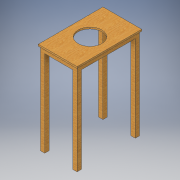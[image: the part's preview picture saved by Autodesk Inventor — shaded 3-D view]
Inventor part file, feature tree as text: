
AUTODESK INVENTOR PART (.ipt)
format: ipt  version: 2018 (Build 220112000, 112)  size: 184,320 bytes
history: native  units: in
note: dims shown in document units (in); Inventor stores cm internally (conversion verified against a paired STEP export)
features: extrude x4, sketch x4
ambient origin geometry x8: Origin, YZ Plane, XZ Plane, XY Plane, X Axis, Y Axis, Z Axis, Center Point
bodies: Solid1 (feature_tree)
feature tree (8):
  extrude  "Extrusion1"  Depth=60.0in
  extrude  "Extrusion2"  Depth=30.0in
  extrude  "Extrusion3"  Depth=4.0in
  extrude  "Extrusion4"  Depth=4.0in
  sketch  "Sketch1"  dims[d0=36.0in d1=60.0in]
  sketch  "Sketch2"  dims[d2=1.5in d3=0.0in d6=30.0in]
  sketch  "Sketch3"  dims[d7=54.0in d8=4.0in]
  sketch  "Sketch4"  dims[d9=4.0in d10=4.0in d11=4.0in d12=4.0in d13=4.0in d14=4.0in d15=4.0in d16=84.0in d17=0.0in d18=2.0in d19=50.0in d20=2.0in d21=4.0in d22=0.0in d23=22.0in d24=4.0in d25=0.0in]
